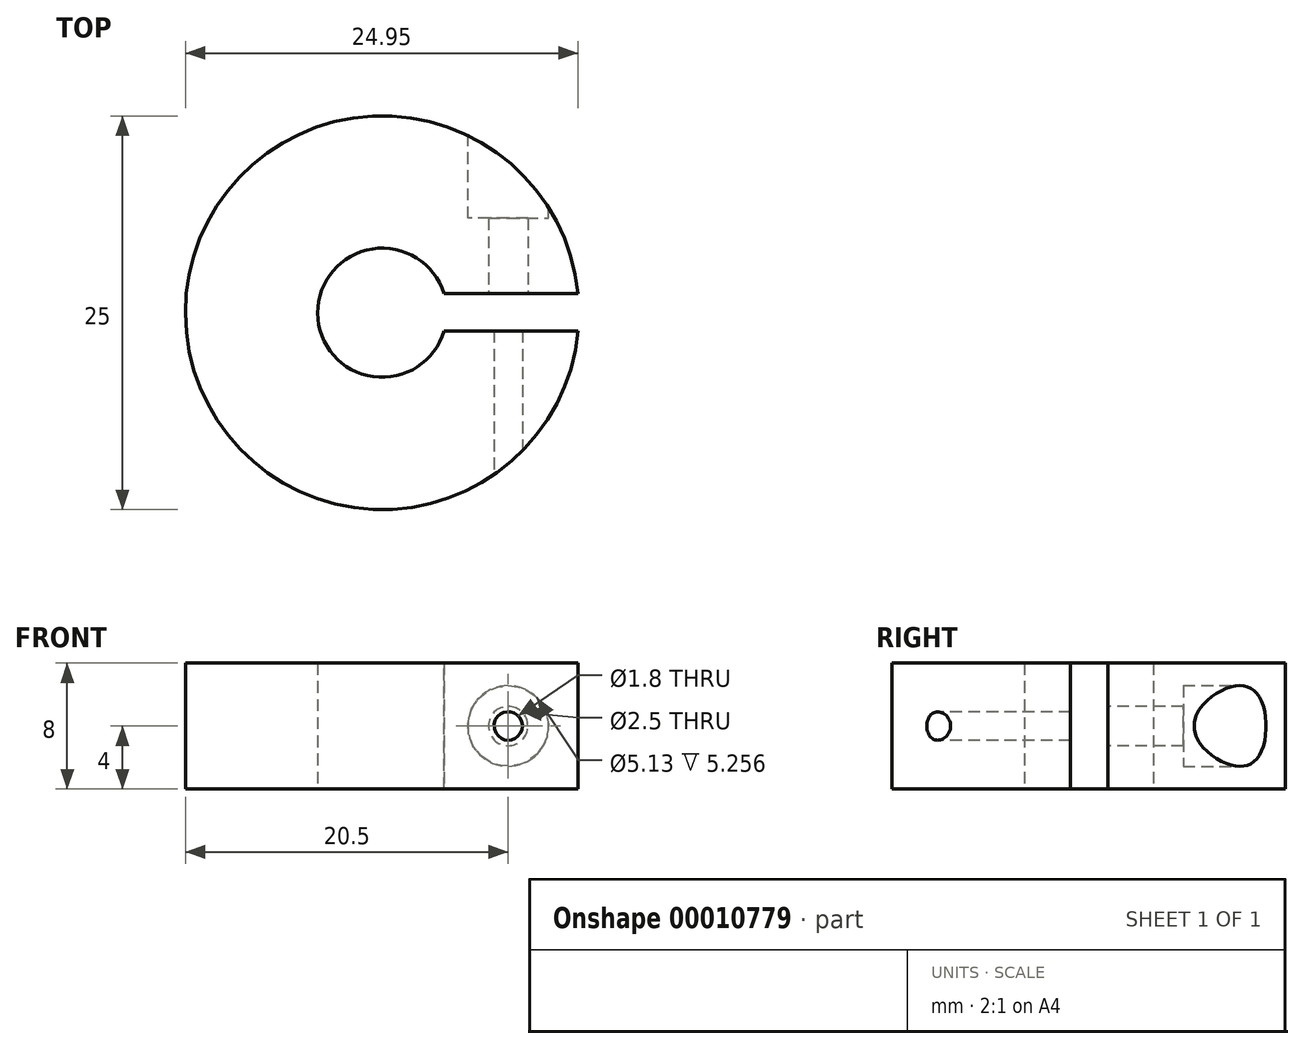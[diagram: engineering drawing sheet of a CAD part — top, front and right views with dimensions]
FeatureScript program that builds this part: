
annotation { "Feature Type Name" : "Feature", "Feature Type Description" : "" }
export const myFeature = defineFeature(function(context is Context, id is Id, definition is map)
    precondition{}
    {
        {
            var Q0;
            Q0=qCreatedBy(makeId("Top.planeOp"),FACE);
            var sketch = newSketch(context, id + "F0", { "sketchPlane" : qUnion([Q0])});
            skCircle(sketch, "E0", {"center": v(0, 0) * mm, "radius": 12.5 * mm});
            skCircle(sketch, "E1", {"center": v(0, 0) * mm, "radius": 4.1 * mm});
            skSolve(sketch);
        }
        {
            var Q0;
            Q0 = qSketchRegion(id + "F0", true);
            extrude(context, id + "F1", {"entities" : qUnion([Q0]), "depth" : 8 * mm});
        }
        {
            var Q0;
            Q0=qCreatedBy(makeId("Front.planeOp"),FACE);
            var sketch = newSketch(context, id + "F2", { "sketchPlane" : qUnion([Q0])});
            skCircle(sketch, "E2", {"center": v(8, 4) * mm, "radius": 0.9 * mm});
            skSolve(sketch);
        }
        {
            var Q0;
            Q0 = qSketchRegion(id + "F2", true);
            extrude(context, id + "F3", {"entities" : qUnion([Q0]), "operationType" : NewBodyOperationType.REMOVE, "endBound" : BoundingType.SYMMETRIC, "oppositeDirection" : true, "depth" : 25 * mm});
        }
        {
            var Q0;
            Q0=makeQuery(id+"F1.opExtrude","CAP_FACE",FACE,{"disambiguationData":[OSD([sQuery(id+"F0.wireOp",EDGE,"E0"),sQuery(id+"F0.wireOp",EDGE,"E1")])],"isStart":false});
            var sketch = newSketch(context, id + "F4", { "sketchPlane" : qUnion([Q0])});
            skLineSegment(sketch, "E3.bottom", {"start": v(3.92, 1.2) * mm, "end": v(13.18, 1.2) * mm});
            skLineSegment(sketch, "E3.top", {"start": v(3.92, -1.16) * mm, "end": v(13.18, -1.16) * mm});
            skLineSegment(sketch, "E3.left", {"start": v(3.92, 1.2) * mm, "end": v(3.92, -1.16) * mm});
            skLineSegment(sketch, "E3.right", {"start": v(13.18, 1.2) * mm, "end": v(13.18, -1.16) * mm});
            skSolve(sketch);
        }
        {
            var Q0;
            Q0 = qSketchRegion(id + "F4", true);
            extrude(context, id + "F5", {"entities" : qUnion([Q0]), "operationType" : NewBodyOperationType.REMOVE, "oppositeDirection" : true, "depth" : 25 * mm});
        }
        {
            var Q0;
            Q0=qCreatedBy(makeId("Front.planeOp"),FACE);
            var sketch = newSketch(context, id + "F6", { "sketchPlane" : qUnion([Q0])});
            skCircle(sketch, "E4", {"center": v(8, 4) * mm, "radius": 1.25 * mm});
            skSolve(sketch);
        }
        {
            var Q0;
            Q0=makeQuery(id+"F6.imprint","IMPRINT",FACE,{"disambiguationData":[TD([[makeQuery(id+"F6.imprint","IMPRINT",EDGE,{"derivedFrom":sQuery(id+"F6.wireOp",EDGE,"E4")}),1.0]])]});
            extrude(context, id + "F7", {"entities" : qUnion([Q0]), "operationType" : NewBodyOperationType.REMOVE, "oppositeDirection" : true, "depth" : 25 * mm});
        }
        {
            var Q0;
            Q0=qCreatedBy(makeId("Front.planeOp"),FACE);
            cPlane(context, id + "F8", {"entities" : qUnion([Q0]), "cplaneType" : CPlaneType.OFFSET, "offset" : 25 * mm, "oppositeDirection" : true, "width" : 150 * mm, "height" : 150 * mm});
        }
        {
            var Q0;
            Q0=qCreatedBy(id+"F8.planeOp",FACE);
            var sketch = newSketch(context, id + "F9", { "sketchPlane" : qUnion([Q0])});
            skCircle(sketch, "E5", {"center": v(8, 4) * mm, "radius": 2.56 * mm});
            skSolve(sketch);
        }
        {
            var Q0;
            Q0 = qSketchRegion(id + "F9", true);
            extrude(context, id + "F10", {"entities" : qUnion([Q0]), "operationType" : NewBodyOperationType.REMOVE, "depth" : 19 * mm});
        }
    });
